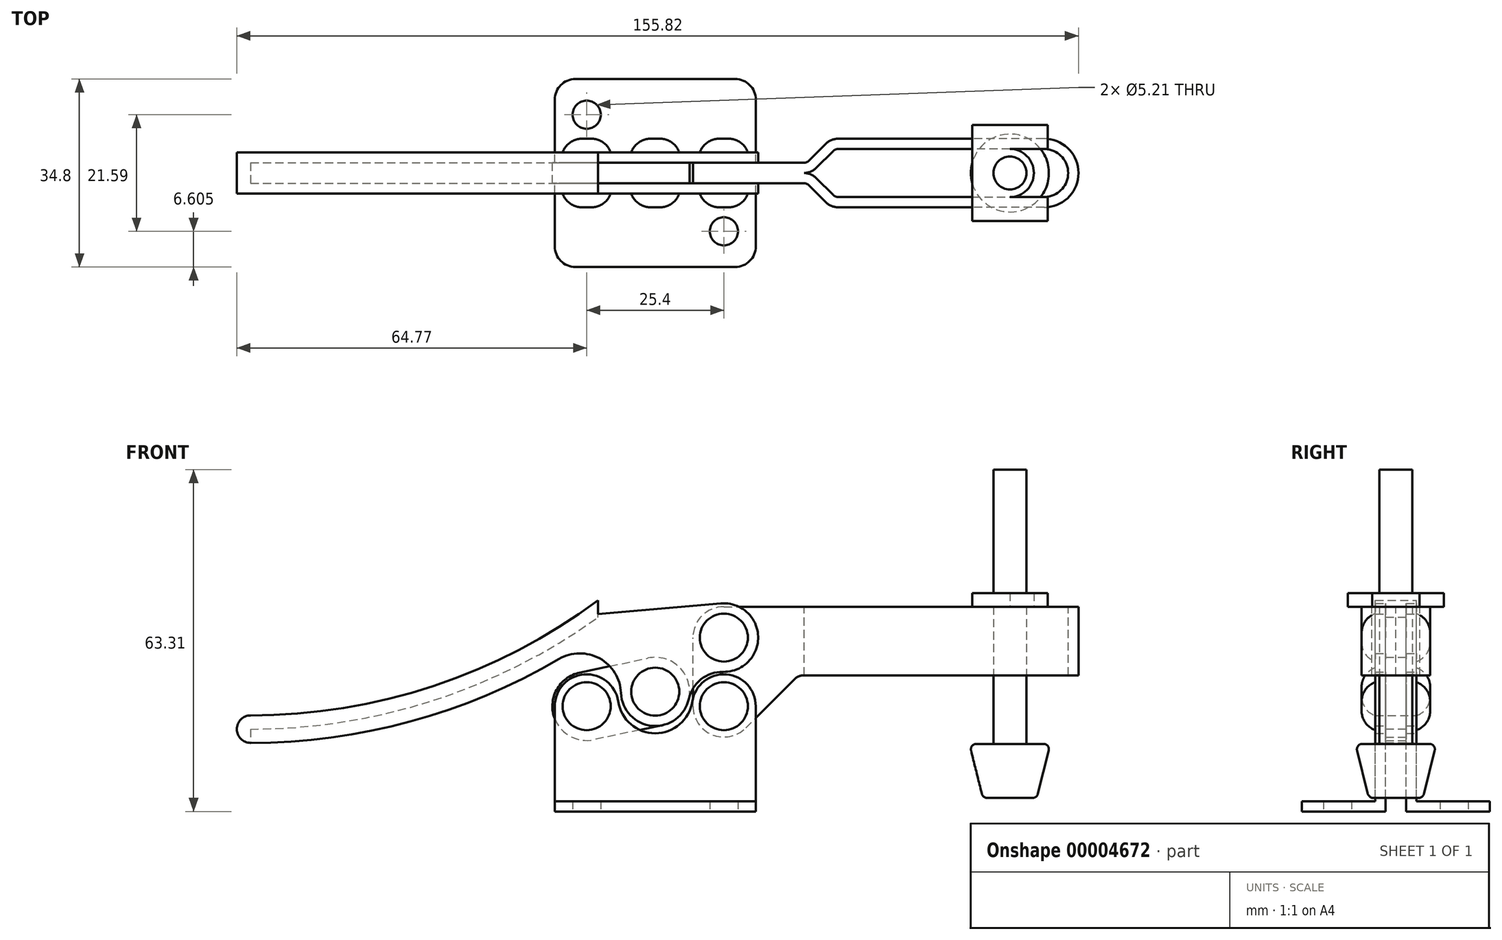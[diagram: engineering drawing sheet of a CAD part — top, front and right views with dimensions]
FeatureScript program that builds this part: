
annotation { "Feature Type Name" : "Feature", "Feature Type Description" : "" }
export const myFeature = defineFeature(function(context is Context, id is Id, definition is map)
    precondition{}
    {
        {
            var Q0;
            Q0=qCreatedBy(makeId("Front.planeOp"),FACE);
            var sketch = newSketch(context, id + "F0", { "sketchPlane" : qUnion([Q0])});
            skLineSegment(sketch, "E0", {"start": v(0, 0) * mm, "end": v(-18.6, 0) * mm});
            skLineSegment(sketch, "E1", {"start": v(-18.6, 0) * mm, "end": v(-18.6, 19.5) * mm});
            skArc(sketch, "E2", {"start": v(-18.6, 19.5) * mm, "mid": v(-13.14, 25.38) * mm, "end": v(-6.86, 20.38) * mm});
            skArc(sketch, "E3", {"start": v(-6.86, 20.38) * mm, "mid": v(-4.52, 16.16) * mm, "end": v(0, 14.48) * mm});
            skArc(sketch, "E4.0.MirrorCS", {"start": v(6.86, 20.38) * mm, "mid": v(4.52, 16.16) * mm, "end": v(0, 14.48) * mm});
            skLineSegment(sketch, "E4.1.MirrorCS", {"start": v(0, 0) * mm, "end": v(18.6, 0) * mm});
            skLineSegment(sketch, "E4.2.MirrorCS", {"start": v(18.6, 0) * mm, "end": v(18.6, 19.5) * mm});
            skArc(sketch, "E4.3.MirrorCS", {"start": v(18.6, 19.5) * mm, "mid": v(13.14, 25.38) * mm, "end": v(6.86, 20.38) * mm});
            skCircle(sketch, "E5", {"center": v(-12.7, 19.5) * mm, "radius": 3.81 * mm});
            skCircle(sketch, "E6.0.MirrorC", {"center": v(12.7, 19.5) * mm, "radius": 3.81 * mm});
            skLineSegment(sketch, "E7", {"start": v(-18.6, 1.9) * mm, "end": v(18.6, 1.9) * mm});
            skSolve(sketch);
        }
        {
            var Q0;
            Q0=qSketchRegion(id+"F0",true);
            extrude(context, id + "F1", {"entities" : qUnion([Q0]), "endBound" : BoundingType.SYMMETRIC, "depth" : 7.62 * mm});
        }
        {
            var Q0;
            {var subQ2=sQuery(id+"F0.wireOp",EDGE,"E0");Q0=makeQuery(id+"F0.imprint","IMPRINT",FACE,{"disambiguationData":[TD([[makeQuery(id+"F0.imprint","IMPRINT",EDGE,{"derivedFrom":subQ2}),-1.0]])]});}
            extrude(context, id + "F2", {"entities" : qUnion([Q0]), "operationType" : NewBodyOperationType.ADD, "endBound" : BoundingType.SYMMETRIC, "depth" : 34.8 * mm});
        }
        {
            var Q0;
            Q0=qSketchRegion(id+"F0",true);
            extrude(context, id + "F3", {"entities" : qUnion([Q0]), "operationType" : NewBodyOperationType.REMOVE, "endBound" : BoundingType.SYMMETRIC, "oppositeDirection" : true, "depth" : 3.8 * mm});
        }
        {
            var Q0;
            Q0=qCreatedBy(makeId("Top.planeOp"),FACE);
            var sketch = newSketch(context, id + "F4", { "sketchPlane" : qUnion([Q0])});
            skCircle(sketch, "E8", {"center": v(-12.7, 10.8) * mm, "radius": 2.6 * mm});
            skArc(sketch, "E9", {"start": v(-14.8, 17.4) * mm, "mid": v(-17.49, 16.28) * mm, "end": v(-18.6, 13.59) * mm});
            skLineSegment(sketch, "E10", {"start": v(-18.6, 13.59) * mm, "end": v(-18.6, 17.4) * mm});
            skLineSegment(sketch, "E11", {"start": v(-18.6, 17.4) * mm, "end": v(-14.8, 17.4) * mm});
            skCircle(sketch, "E12.0.MirrorC", {"center": v(12.7, 10.8) * mm, "radius": 2.6 * mm});
            skLineSegment(sketch, "E12.1.MirrorCS", {"start": v(18.6, 17.4) * mm, "end": v(14.8, 17.4) * mm});
            skLineSegment(sketch, "E12.2.MirrorCS", {"start": v(18.6, 13.59) * mm, "end": v(18.6, 17.4) * mm});
            skArc(sketch, "E12.3.MirrorCS", {"start": v(14.8, 17.4) * mm, "mid": v(17.49, 16.28) * mm, "end": v(18.6, 13.59) * mm});
            skLineSegment(sketch, "E13.0.MirrorCS", {"start": v(-18.6, -13.59) * mm, "end": v(-18.6, -17.4) * mm});
            skArc(sketch, "E13.1.MirrorCS", {"start": v(-14.8, -17.4) * mm, "mid": v(-17.49, -16.28) * mm, "end": v(-18.6, -13.59) * mm});
            skCircle(sketch, "E13.2.MirrorC", {"center": v(12.7, -10.8) * mm, "radius": 2.6 * mm});
            skCircle(sketch, "E13.3.MirrorC", {"center": v(-12.7, -10.8) * mm, "radius": 2.6 * mm});
            skArc(sketch, "E13.4.MirrorCS", {"start": v(14.8, -17.4) * mm, "mid": v(17.49, -16.28) * mm, "end": v(18.6, -13.59) * mm});
            skLineSegment(sketch, "E13.5.MirrorCS", {"start": v(-18.6, -17.4) * mm, "end": v(-14.8, -17.4) * mm});
            skLineSegment(sketch, "E13.6.MirrorCS", {"start": v(18.6, -17.4) * mm, "end": v(14.8, -17.4) * mm});
            skLineSegment(sketch, "E13.7.MirrorCS", {"start": v(18.6, -13.59) * mm, "end": v(18.6, -17.4) * mm});
            skSolve(sketch);
        }
        {
            var Q0;
            Q0=makeQuery(id+"F4.imprint","IMPRINT",FACE,{"disambiguationData":[TD([[makeQuery(id+"F4.imprint","IMPRINT",EDGE,{"derivedFrom":sQuery(id+"F4.wireOp",EDGE,"E8")}),1.0]])]});
            var Q1;
            Q1=makeQuery(id+"F4.imprint","IMPRINT",FACE,{"disambiguationData":[TD([[makeQuery(id+"F4.imprint","IMPRINT",EDGE,{"derivedFrom":sQuery(id+"F4.wireOp",EDGE,"E9")}),-1.0]])]});
            var Q2;
            Q2=makeQuery(id+"F4.imprint","IMPRINT",FACE,{"disambiguationData":[TD([[makeQuery(id+"F4.imprint","IMPRINT",EDGE,{"derivedFrom":sQuery(id+"F4.wireOp",EDGE,"E12.0.MirrorC")}),-1.0]])]});
            var Q3;
            Q3=makeQuery(id+"F4.imprint","IMPRINT",FACE,{"disambiguationData":[TD([[makeQuery(id+"F4.imprint","IMPRINT",EDGE,{"derivedFrom":sQuery(id+"F4.wireOp",EDGE,"E12.1.MirrorCS")}),1.0]])]});
            var Q4;
            Q4=makeQuery(id+"F4.imprint","IMPRINT",FACE,{"disambiguationData":[TD([[makeQuery(id+"F4.imprint","IMPRINT",EDGE,{"derivedFrom":sQuery(id+"F4.wireOp",EDGE,"E13.2.MirrorC")}),1.0]])]});
            var Q5;
            Q5=makeQuery(id+"F4.imprint","IMPRINT",FACE,{"disambiguationData":[TD([[makeQuery(id+"F4.imprint","IMPRINT",EDGE,{"derivedFrom":sQuery(id+"F4.wireOp",EDGE,"E13.4.MirrorCS")}),-1.0]])]});
            var Q6;
            Q6=makeQuery(id+"F4.imprint","IMPRINT",FACE,{"disambiguationData":[TD([[makeQuery(id+"F4.imprint","IMPRINT",EDGE,{"derivedFrom":sQuery(id+"F4.wireOp",EDGE,"E13.0.MirrorCS")}),1.0]])]});
            var Q7;
            Q7=makeQuery(id+"F4.imprint","IMPRINT",FACE,{"disambiguationData":[TD([[makeQuery(id+"F4.imprint","IMPRINT",EDGE,{"derivedFrom":sQuery(id+"F4.wireOp",EDGE,"E13.3.MirrorC")}),-1.0]])]});
            extrude(context, id + "F5", {"entities" : qUnion([Q0, Q1, Q2, Q3, Q4, Q5, Q6, Q7]), "operationType" : NewBodyOperationType.REMOVE, "endBound" : BoundingType.THROUGH_ALL, "depth" : 25.4 * mm});
        }
        {
            var Q0;
            Q0=qCreatedBy(makeId("Front.planeOp"),FACE);
            var sketch = newSketch(context, id + "F6", { "sketchPlane" : qUnion([Q0])});
            skCircle(sketch, "E14", {"center": v(12.7, 19.5) * mm, "radius": 5.72 * mm});
            skLineSegment(sketch, "E15", {"start": v(6.98, 19.5) * mm, "end": v(6.98, 32.2) * mm});
            skCircle(sketch, "E16", {"center": v(12.7, 32.2) * mm, "radius": 5.72 * mm});
            skLineSegment(sketch, "E17", {"start": v(12.7, 37.9) * mm, "end": v(75.8, 37.9) * mm});
            skLineSegment(sketch, "E18", {"start": v(16.74, 15.45) * mm, "end": v(25.75, 24.47) * mm});
            skArc(sketch, "E19", {"start": v(25.75, 24.47) * mm, "mid": v(26.58, 25.02) * mm, "end": v(27.55, 25.2) * mm});
            skLineSegment(sketch, "E20", {"start": v(27.55, 25.2) * mm, "end": v(75.8, 25.2) * mm});
            skLineSegment(sketch, "E21", {"start": v(27.55, 25.2) * mm, "end": v(27.55, 37.9) * mm});
            skArc(sketch, "E22", {"start": v(75.8, 25.2) * mm, "mid": v(77.6, 25.95) * mm, "end": v(78.35, 27.75) * mm});
            skArc(sketch, "E23", {"start": v(75.8, 37.9) * mm, "mid": v(77.6, 37.17) * mm, "end": v(78.35, 35.37) * mm});
            skLineSegment(sketch, "E24", {"start": v(78.35, 35.37) * mm, "end": v(78.35, 27.75) * mm});
            skCircle(sketch, "E25", {"center": v(-12.7, 19.5) * mm, "radius": 3.81 * mm});
            skCircle(sketch, "E26", {"center": v(0, 22.18) * mm, "radius": 3.81 * mm});
            skCircle(sketch, "E27", {"center": v(-12.7, 19.5) * mm, "radius": 6.35 * mm});
            skCircle(sketch, "E28", {"center": v(0, 22.18) * mm, "radius": 6.35 * mm});
            skLineSegment(sketch, "E29", {"start": v(-14.01, 25.7) * mm, "end": v(-1.31, 28.4) * mm});
            skLineSegment(sketch, "E30", {"start": v(1.31, 15.97) * mm, "end": v(-11.39, 13.28) * mm});
            skSolve(sketch);
        }
        {
            var Q0;
            {var subQ0=sQuery(id+"F6.wireOp",EDGE,"E14");var subQ2=makeQuery(id+"F6.imprint","INTERSECT",VERTEX,{"derivedFrom":[subQ0,sQuery(id+"F6.wireOp",EDGE,"E15")]});Q0=makeQuery(id+"F6.imprint","IMPRINT",FACE,{"disambiguationData":[TD([[makeQuery(id+"F6.imprint","IMPRINT",EDGE,{"disambiguationData":[TD([[subQ2,-1.0]])],"derivedFrom":subQ0}),1.0]])]});}
            var Q1;
            {var subQ0=sQuery(id+"F6.wireOp",EDGE,"E16");var subQ2=makeQuery(id+"F6.imprint","INTERSECT",VERTEX,{"derivedFrom":[sQuery(id+"F6.wireOp",EDGE,"E15"),subQ0]});Q1=makeQuery(id+"F6.imprint","IMPRINT",FACE,{"disambiguationData":[TD([[makeQuery(id+"F6.imprint","IMPRINT",EDGE,{"disambiguationData":[TD([[subQ2,1.0]])],"derivedFrom":subQ0}),1.0]])]});}
            var Q2;
            {var subQ5=sQuery(id+"F6.wireOp",EDGE,"E15");Q2=makeQuery(id+"F6.imprint","IMPRINT",FACE,{"disambiguationData":[TD([[makeQuery(id+"F6.imprint","IMPRINT",EDGE,{"derivedFrom":subQ5}),-1.0]])]});}
            var Q3;
            {var subQ1=sQuery(id+"F6.wireOp",EDGE,"E29");Q3=makeQuery(id+"F6.imprint","IMPRINT",FACE,{"disambiguationData":[TD([[makeQuery(id+"F6.imprint","IMPRINT",EDGE,{"derivedFrom":subQ1}),-1.0]])]});}
            var Q4;
            Q4=makeQuery(id+"F6.imprint","IMPRINT",FACE,{"disambiguationData":[TD([[makeQuery(id+"F6.imprint","IMPRINT",EDGE,{"derivedFrom":sQuery(id+"F6.wireOp",EDGE,"E26")}),-1.0]])]});
            var Q5;
            Q5=makeQuery(id+"F6.imprint","IMPRINT",FACE,{"disambiguationData":[TD([[makeQuery(id+"F6.imprint","IMPRINT",EDGE,{"derivedFrom":sQuery(id+"F6.wireOp",EDGE,"E25")}),-1.0]])]});
            extrude(context, id + "F7", {"entities" : qUnion([Q0, Q1, Q2, Q3, Q4, Q5]), "operationType" : NewBodyOperationType.ADD, "endBound" : BoundingType.SYMMETRIC, "depth" : 3.8 * mm});
        }
        {
            var Q0;
            Q0=makeQuery(id+"F7.opExtrude","SWEPT_FACE",FACE,{"disambiguationData":[OSD([sQuery(id+"F6.wireOp",EDGE,"E17")])]});
            var sketch = newSketch(context, id + "F8", { "sketchPlane" : qUnion([Q0])});
            skLineSegment(sketch, "E31", {"start": v(12.7, 1.9) * mm, "end": v(27.55, 1.9) * mm});
            skArc(sketch, "E32", {"start": v(27.55, 1.9) * mm, "mid": v(28.04, 2) * mm, "end": v(28.45, 2.28) * mm});
            skLineSegment(sketch, "E33", {"start": v(27.55, 0) * mm, "end": v(12.7, 0) * mm});
            skArc(sketch, "E34", {"start": v(27.55, 0) * mm, "mid": v(28.76, 0.24) * mm, "end": v(29.8, 0.93) * mm});
            skLineSegment(sketch, "E35", {"start": v(28.45, 2.28) * mm, "end": v(31.6, 5.42) * mm});
            skLineSegment(sketch, "E36", {"start": v(29.8, 0.93) * mm, "end": v(32.94, 4.07) * mm});
            skLineSegment(sketch, "E37", {"start": v(33.84, 4.44) * mm, "end": v(72, 4.44) * mm});
            skLineSegment(sketch, "E38", {"start": v(72, 6.35) * mm, "end": v(33.84, 6.35) * mm});
            skArc(sketch, "E39", {"start": v(32.94, 4.07) * mm, "mid": v(33.35, 4.35) * mm, "end": v(33.84, 4.44) * mm});
            skArc(sketch, "E40", {"start": v(31.6, 5.42) * mm, "mid": v(32.62, 6.1) * mm, "end": v(33.84, 6.35) * mm});
            skArc(sketch, "E41", {"start": v(72, 4.44) * mm, "mid": v(75.14, 3.14) * mm, "end": v(76.44, 0) * mm});
            skArc(sketch, "E42", {"start": v(72, 6.35) * mm, "mid": v(76.49, 4.5) * mm, "end": v(78.35, 0) * mm});
            skLineSegment(sketch, "E43", {"start": v(76.44, 0) * mm, "end": v(78.35, 0) * mm});
            skArc(sketch, "E44.0.MirrorCS", {"start": v(72, -4.45) * mm, "mid": v(75.14, -3.14) * mm, "end": v(76.44, 0) * mm});
            skArc(sketch, "E44.1.MirrorCS", {"start": v(31.6, -5.42) * mm, "mid": v(32.62, -6.1) * mm, "end": v(33.84, -6.35) * mm});
            skLineSegment(sketch, "E44.3.MirrorCS", {"start": v(29.8, -0.93) * mm, "end": v(32.94, -4.07) * mm});
            skArc(sketch, "E44.4.MirrorCS", {"start": v(72, -6.35) * mm, "mid": v(76.49, -4.5) * mm, "end": v(78.35, 0) * mm});
            skArc(sketch, "E44.5.MirrorCS", {"start": v(27.55, -1.9) * mm, "mid": v(28.04, -2) * mm, "end": v(28.45, -2.28) * mm});
            skLineSegment(sketch, "E44.6.MirrorCS", {"start": v(33.84, -4.44) * mm, "end": v(72, -4.44) * mm});
            skLineSegment(sketch, "E44.7.MirrorCS", {"start": v(72, -6.35) * mm, "end": v(33.84, -6.35) * mm});
            skLineSegment(sketch, "E44.8.MirrorCS", {"start": v(28.45, -2.28) * mm, "end": v(31.6, -5.42) * mm});
            skArc(sketch, "E44.9.MirrorCS", {"start": v(32.94, -4.07) * mm, "mid": v(33.35, -4.35) * mm, "end": v(33.84, -4.44) * mm});
            skArc(sketch, "E44.10.MirrorCS", {"start": v(27.55, 0) * mm, "mid": v(28.76, -0.24) * mm, "end": v(29.8, -0.93) * mm});
            skSolve(sketch);
        }
        {
            var Q0;
            Q0=makeQuery(id+"F8.imprint","IMPRINT",FACE,{"disambiguationData":[TD([[makeQuery(id+"F8.imprint","IMPRINT",EDGE,{"derivedFrom":sQuery(id+"F8.wireOp",EDGE,"E44.0.MirrorCS")}),-1.0]])]});
            var Q1;
            {var subQ2=sQuery(id+"F8.wireOp",EDGE,"E32");Q1=makeQuery(id+"F8.imprint","IMPRINT",FACE,{"disambiguationData":[TD([[makeQuery(id+"F8.imprint","IMPRINT",EDGE,{"derivedFrom":subQ2}),-1.0]])]});}
            var Q2;
            Q2=makeQuery(id+"F8.imprint","IMPRINT",FACE,{"disambiguationData":[TD([[makeQuery(id+"F8.imprint","IMPRINT",EDGE,{"derivedFrom":sQuery(id+"F8.wireOp",EDGE,"E34")}),-1.0]])]});
            extrude(context, id + "F9", {"entities" : qUnion([Q0, Q1, Q2]), "operationType" : NewBodyOperationType.ADD, "oppositeDirection" : true, "depth" : 12.7 * mm});
        }
        {
            var Q0;
            Q0=makeQuery(id+"F8.imprint","IMPRINT",FACE,{"disambiguationData":[TD([[makeQuery(id+"F8.imprint","IMPRINT",EDGE,{"derivedFrom":sQuery(id+"F8.wireOp",EDGE,"E34")}),-1.0]])]});
            extrude(context, id + "F10", {"entities" : qUnion([Q0]), "operationType" : NewBodyOperationType.REMOVE, "endBound" : BoundingType.THROUGH_ALL, "oppositeDirection" : true, "depth" : 25.4 * mm});
        }
        {
            var Q0;
            Q0=qCreatedBy(makeId("Front.planeOp"),FACE);
            var sketch = newSketch(context, id + "F11", { "sketchPlane" : qUnion([Q0])});
            skCircle(sketch, "E45", {"center": v(12.7, 32.2) * mm, "radius": 6.35 * mm});
            skCircle(sketch, "E46", {"center": v(0, 22.18) * mm, "radius": 6.35 * mm});
            skArc(sketch, "E47", {"start": v(12.56, 25.85) * mm, "mid": v(8.48, 24.48) * mm, "end": v(6.2, 20.84) * mm});
            skArc(sketch, "E48", {"start": v(-6.35, 21.94) * mm, "mid": v(-10.3, 28.33) * mm, "end": v(-17.82, 28.22) * mm});
            skArc(sketch, "E49", {"start": v(-17.82, 28.22) * mm, "mid": v(-45.34, 16.65) * mm, "end": v(-74.93, 12.7) * mm});
            skArc(sketch, "E50", {"start": v(-74.93, 12.7) * mm, "mid": v(-77.47, 15.24) * mm, "end": v(-74.93, 17.78) * mm});
            skArc(sketch, "E51", {"start": v(-74.93, 17.78) * mm, "mid": v(-41.06, 23.24) * mm, "end": v(-10.63, 39.07) * mm});
            skLineSegment(sketch, "E52", {"start": v(12.15, 38.52) * mm, "end": v(-10.63, 36.53) * mm});
            skLineSegment(sketch, "E53", {"start": v(-10.63, 36.53) * mm, "end": v(-10.63, 39.07) * mm});
            skArc(sketch, "E54", {"start": v(-74.93, 15.24) * mm, "mid": v(-41.16, 20.54) * mm, "end": v(-10.63, 35.92) * mm});
            skLineSegment(sketch, "E55", {"start": v(-10.63, 36.53) * mm, "end": v(-10.63, 35.92) * mm});
            skLineSegment(sketch, "E56", {"start": v(-74.93, 15.24) * mm, "end": v(-74.93, 17.78) * mm});
            skLineSegment(sketch, "E57", {"start": v(6.33, 22.73) * mm, "end": v(5, 37.9) * mm});
            skLineSegment(sketch, "E58", {"start": v(15.47, 37.9) * mm, "end": v(12.7, 37.9) * mm});
            skLineSegment(sketch, "E59", {"start": v(6.98, 29.43) * mm, "end": v(6.98, 32.2) * mm});
            skArc(sketch, "E60", {"start": v(12.7, 37.9) * mm, "mid": v(8.66, 36.24) * mm, "end": v(6.99, 32.2) * mm});
            skLineSegment(sketch, "E61", {"start": v(6.98, 29.43) * mm, "end": v(6.98, 22.8) * mm});
            skSolve(sketch);
        }
        {
            var Q0;
            {var subQ0=sQuery(id+"F11.wireOp",EDGE,"E46");var subQ3=makeQuery(id+"F11.imprint","INTERSECT",VERTEX,{"derivedFrom":[subQ0,sQuery(id+"F11.wireOp",EDGE,"E48")]});Q0=makeQuery(id+"F11.imprint","IMPRINT",FACE,{"disambiguationData":[TD([[makeQuery(id+"F11.imprint","IMPRINT",EDGE,{"disambiguationData":[TD([[subQ3,1.0]])],"derivedFrom":subQ0}),1.0]])]});}
            var Q1;
            Q1=makeQuery(id+"F11.imprint","IMPRINT",FACE,{"disambiguationData":[TD([[makeQuery(id+"F11.imprint","IMPRINT",EDGE,{"derivedFrom":sQuery(id+"F11.wireOp",EDGE,"E51")}),-1.0]])]});
            var Q2;
            {var subQ3=sQuery(id+"F11.wireOp",EDGE,"E48");Q2=makeQuery(id+"F11.imprint","IMPRINT",FACE,{"disambiguationData":[TD([[makeQuery(id+"F11.imprint","IMPRINT",EDGE,{"derivedFrom":subQ3}),-1.0]])]});}
            var Q3;
            {var subQ0=sQuery(id+"F11.wireOp",EDGE,"E61");Q3=makeQuery(id+"F11.imprint","IMPRINT",FACE,{"disambiguationData":[TD([[makeQuery(id+"F11.imprint","IMPRINT",EDGE,{"derivedFrom":subQ0}),1.0]])]});}
            var Q4;
            {var subQ1=sQuery(id+"F11.wireOp",EDGE,"E58");Q4=makeQuery(id+"F11.imprint","IMPRINT",FACE,{"disambiguationData":[TD([[makeQuery(id+"F11.imprint","IMPRINT",EDGE,{"derivedFrom":subQ1}),1.0]])]});}
            var Q5;
            {var subQ1=sQuery(id+"F11.wireOp",EDGE,"E58");Q5=makeQuery(id+"F11.imprint","IMPRINT",FACE,{"disambiguationData":[TD([[makeQuery(id+"F11.imprint","IMPRINT",EDGE,{"derivedFrom":subQ1}),-1.0]])]});}
            var Q6;
            {var subQ1=sQuery(id+"F11.wireOp",EDGE,"E57");Q6=makeQuery(id+"F11.imprint","IMPRINT",FACE,{"disambiguationData":[TD([[makeQuery(id+"F11.imprint","IMPRINT",EDGE,{"derivedFrom":subQ1}),-1.0]])]});}
            extrude(context, id + "F12", {"entities" : qUnion([Q0, Q1, Q2, Q3, Q4, Q5, Q6]), "operationType" : NewBodyOperationType.ADD, "endBound" : BoundingType.SYMMETRIC, "depth" : 7.62 * mm});
        }
        {
            var Q0;
            Q0=qCreatedBy(makeId("Front.planeOp"),FACE);
            var sketch = newSketch(context, id + "F13", { "sketchPlane" : qUnion([Q0])});
            skCircle(sketch, "E62", {"center": v(12.7, 32.2) * mm, "radius": 4.45 * mm});
            skCircle(sketch, "E63", {"center": v(12.7, 19.5) * mm, "radius": 4.45 * mm});
            skCircle(sketch, "E64", {"center": v(0, 22.18) * mm, "radius": 4.45 * mm});
            skCircle(sketch, "E65", {"center": v(-12.7, 19.5) * mm, "radius": 4.45 * mm});
            skSolve(sketch);
        }
        {
            var Q0;
            {Q0=qUnion([makeQuery(id+"F13.imprint","IMPRINT",FACE,{"disambiguationData":[TD([[makeQuery(id+"F13.imprint","IMPRINT",EDGE,{"derivedFrom":sQuery(id+"F13.wireOp",EDGE,"E62")}),1.0]])]}),makeQuery(id+"F13.imprint","IMPRINT",FACE,{"disambiguationData":[TD([[makeQuery(id+"F13.imprint","IMPRINT",EDGE,{"derivedFrom":sQuery(id+"F13.wireOp",EDGE,"E63")}),1.0]])]}),makeQuery(id+"F13.imprint","IMPRINT",FACE,{"disambiguationData":[TD([[makeQuery(id+"F13.imprint","IMPRINT",EDGE,{"derivedFrom":sQuery(id+"F13.wireOp",EDGE,"E64")}),1.0]])]}),makeQuery(id+"F13.imprint","IMPRINT",FACE,{"disambiguationData":[TD([[makeQuery(id+"F13.imprint","IMPRINT",EDGE,{"derivedFrom":sQuery(id+"F13.wireOp",EDGE,"E65")}),1.0]])]})]);}
            extrude(context, id + "F14", {"entities" : qUnion([Q0]), "operationType" : NewBodyOperationType.ADD, "endBound" : BoundingType.SYMMETRIC, "depth" : 12.7 * mm});
        }
        {
            var Q0;
            Q0=qCreatedBy(makeId("Front.planeOp"),FACE);
            var sketch = newSketch(context, id + "F15", { "sketchPlane" : qUnion([Q0])});
            skLineSegment(sketch, "E66", {"start": v(-8.43, 26.89) * mm, "end": v(-1.31, 28.4) * mm});
            skArc(sketch, "E67", {"start": v(6.2, 20.84) * mm, "mid": v(4.5, 26.66) * mm, "end": v(-1.31, 28.4) * mm});
            skArc(sketch, "E68", {"start": v(6.98, 22.8) * mm, "mid": v(6.51, 21.85) * mm, "end": v(6.2, 20.84) * mm});
            skLineSegment(sketch, "E69", {"start": v(6.98, 22.8) * mm, "end": v(6.98, 32.2) * mm});
            skArc(sketch, "E70", {"start": v(12.7, 37.9) * mm, "mid": v(8.66, 36.24) * mm, "end": v(6.99, 32.2) * mm});
            skLineSegment(sketch, "E71", {"start": v(12.7, 37.9) * mm, "end": v(15.47, 37.9) * mm});
            skArc(sketch, "E72", {"start": v(15.47, 37.9) * mm, "mid": v(13.85, 38.44) * mm, "end": v(12.15, 38.52) * mm});
            skLineSegment(sketch, "E73", {"start": v(12.15, 38.52) * mm, "end": v(-10.63, 36.53) * mm});
            skLineSegment(sketch, "E74", {"start": v(-10.63, 35.92) * mm, "end": v(-10.63, 36.53) * mm});
            skArc(sketch, "E75", {"start": v(-8.43, 26.89) * mm, "mid": v(-12.89, 29.2) * mm, "end": v(-17.82, 28.22) * mm});
            skArc(sketch, "E76", {"start": v(-74.93, 15.24) * mm, "mid": v(-41.16, 20.54) * mm, "end": v(-10.63, 35.92) * mm});
            skArc(sketch, "E77", {"start": v(-74.93, 12.7) * mm, "mid": v(-45.34, 16.65) * mm, "end": v(-17.82, 28.22) * mm});
            skLineSegment(sketch, "E78", {"start": v(-74.93, 15.24) * mm, "end": v(-74.93, 12.7) * mm});
            skSolve(sketch);
        }
        {
            var Q0;
            Q0=makeQuery(id+"F15.imprint","IMPRINT",FACE,{"disambiguationData":[TD([[makeQuery(id+"F15.imprint","IMPRINT",EDGE,{"derivedFrom":sQuery(id+"F15.wireOp",EDGE,"E66")}),1.0]])]});
            extrude(context, id + "F16", {"entities" : qUnion([Q0]), "operationType" : NewBodyOperationType.REMOVE, "endBound" : BoundingType.SYMMETRIC, "oppositeDirection" : true, "depth" : 3.8 * mm});
        }
        {
            var Q0;
            Q0=makeQuery(id+"F14.opExtrude","CAP_FACE",FACE,{"disambiguationData":[OSD([sQuery(id+"F13.wireOp",EDGE,"E65")])],"isStart":false});
            var Q1;
            Q1=makeQuery(id+"F14.opExtrude","CAP_FACE",FACE,{"disambiguationData":[OSD([sQuery(id+"F13.wireOp",EDGE,"E64")])],"isStart":false});
            var Q2;
            Q2=makeQuery(id+"F14.opExtrude","CAP_FACE",FACE,{"disambiguationData":[OSD([sQuery(id+"F13.wireOp",EDGE,"E63")])],"isStart":false});
            var Q3;
            Q3=makeQuery(id+"F14.opExtrude","CAP_FACE",FACE,{"disambiguationData":[OSD([sQuery(id+"F13.wireOp",EDGE,"E62")])],"isStart":false});
            var Q4;
            Q4=makeQuery(id+"F14.opExtrude","CAP_FACE",FACE,{"disambiguationData":[OSD([sQuery(id+"F13.wireOp",EDGE,"E62")])],"isStart":true});
            var Q5;
            Q5=makeQuery(id+"F14.opExtrude","CAP_FACE",FACE,{"disambiguationData":[OSD([sQuery(id+"F13.wireOp",EDGE,"E63")])],"isStart":true});
            var Q6;
            Q6=makeQuery(id+"F14.opExtrude","CAP_FACE",FACE,{"disambiguationData":[OSD([sQuery(id+"F13.wireOp",EDGE,"E64")])],"isStart":true});
            var Q7;
            Q7=makeQuery(id+"F14.opExtrude","CAP_FACE",FACE,{"disambiguationData":[OSD([sQuery(id+"F13.wireOp",EDGE,"E65")])],"isStart":true});
            fillet(context, id + "F17", {"entities" : qUnion([Q0, Q1, Q2, Q3, Q4, Q5, Q6, Q7]), "radius" : 3.8 * mm, "tangentPropagation" : true, "allowEdgeOverflow" : false});
        }
        {
            var Q0;
            {var subQ0=sQuery(id+"F6.wireOp",EDGE,"E17");Q0=makeQuery(id+"F16.boolean.opBoolean","MERGE",FACE,{"derivedFrom":[makeQuery(id+"F9.boolean.opBoolean","MERGE",FACE,{"derivedFrom":[makeQuery(id+"F7.opExtrude","SWEPT_FACE",FACE,{"disambiguationData":[OSD([subQ0])]}),makeQuery(id+"F9.opExtrude","CAP_FACE",FACE,{"disambiguationData":[OSD([subQ0,sQuery(id+"F6.wireOp",EDGE,"E21"),sQuery(id+"F8.wireOp",EDGE,"E32"),sQuery(id+"F8.wireOp",EDGE,"E35"),sQuery(id+"F8.wireOp",EDGE,"E38"),sQuery(id+"F8.wireOp",EDGE,"E40"),sQuery(id+"F8.wireOp",EDGE,"E42"),sQuery(id+"F8.wireOp",EDGE,"E44.1.MirrorCS"),sQuery(id+"F8.wireOp",EDGE,"E44.4.MirrorCS"),sQuery(id+"F8.wireOp",EDGE,"E44.5.MirrorCS"),sQuery(id+"F8.wireOp",EDGE,"E44.7.MirrorCS"),sQuery(id+"F8.wireOp",EDGE,"E44.8.MirrorCS")])],"isStart":true})]}),makeQuery(id+"F16.opExtrude","SWEPT_FACE",FACE,{"disambiguationData":[OSD([sQuery(id+"F15.wireOp",EDGE,"E71")])]})]});}
            var sketch = newSketch(context, id + "F18", { "sketchPlane" : qUnion([Q0])});
            skCircle(sketch, "E79", {"center": v(65.65, 0) * mm, "radius": 4.44 * mm});
            skCircle(sketch, "E80", {"center": v(65.65, 0) * mm, "radius": 3.05 * mm});
            skLineSegment(sketch, "E81", {"start": v(65.65, -4.44) * mm, "end": v(65.65, 4.44) * mm});
            skLineSegment(sketch, "E82.rect.bottom", {"start": v(58.66, -8.89) * mm, "end": v(72.63, -8.89) * mm});
            skLineSegment(sketch, "E82.rect.top", {"start": v(58.66, 8.89) * mm, "end": v(72.63, 8.89) * mm});
            skLineSegment(sketch, "E82.rect.left", {"start": v(58.66, -8.89) * mm, "end": v(58.66, 8.89) * mm});
            skLineSegment(sketch, "E82.rect.right", {"start": v(72.63, -8.89) * mm, "end": v(72.63, 8.89) * mm});
            skSolve(sketch);
        }
        {
            var Q0;
            {var subQ0=sQuery(id+"F18.wireOp",EDGE,"E81");var subQ1=sQuery(id+"F18.wireOp",EDGE,"E80");var subQ3=makeQuery(id+"F18.imprint","INTERSECT",VERTEX,{"disambiguationData":[OD(0.0)],"derivedFrom":[subQ1,subQ0]});Q0=makeQuery(id+"F18.imprint","IMPRINT",FACE,{"disambiguationData":[TD([[makeQuery(id+"F18.imprint","IMPRINT",EDGE,{"disambiguationData":[TD([[subQ3,1.0]])],"derivedFrom":subQ1}),1.0]])]});}
            var Q1;
            {var subQ0=sQuery(id+"F18.wireOp",EDGE,"E81");var subQ1=sQuery(id+"F18.wireOp",EDGE,"E80");var subQ3=makeQuery(id+"F18.imprint","INTERSECT",VERTEX,{"disambiguationData":[OD(0.0)],"derivedFrom":[subQ1,subQ0]});Q1=makeQuery(id+"F18.imprint","IMPRINT",FACE,{"disambiguationData":[TD([[makeQuery(id+"F18.imprint","IMPRINT",EDGE,{"disambiguationData":[TD([[subQ3,-1.0]])],"derivedFrom":subQ1}),1.0]])]});}
            extrude(context, id + "F19", {"entities" : qUnion([Q0, Q1]), "operationType" : NewBodyOperationType.ADD, "endBound" : BoundingType.SYMMETRIC, "depth" : 50.8 * mm});
        }
        {
            var Q0;
            Q0=makeQuery(id+"F19.opExtrude","CAP_FACE",FACE,{"disambiguationData":[OSD([sQuery(id+"F18.wireOp",EDGE,"E80")])],"isStart":true});
            var sketch = newSketch(context, id + "F20", { "sketchPlane" : qUnion([Q0])});
            skLineSegment(sketch, "E83", {"start": v(65.65, 0) * mm, "end": v(62.6, 0) * mm});
            skSolve(sketch);
        }
        {
            var Q0;
            Q0=qCreatedBy(makeId("Front.planeOp"),FACE);
            var sketch = newSketch(context, id + "F21", { "sketchPlane" : qUnion([Q0])});
            skLineSegment(sketch, "E84", {"start": v(65.65, 12.5) * mm, "end": v(58.15, 12.5) * mm});
            skLineSegment(sketch, "E85", {"start": v(58.15, 12.5) * mm, "end": v(60.65, 2.5) * mm});
            skLineSegment(sketch, "E86", {"start": v(60.65, 2.5) * mm, "end": v(65.65, 2.5) * mm});
            skLineSegment(sketch, "E87", {"start": v(65.65, 2.5) * mm, "end": v(65.65, 12.5) * mm});
            skSolve(sketch);
        }
        {
            var Q0;
            Q0=makeQuery(id+"F21.imprint","IMPRINT",FACE,{"disambiguationData":[TD([[makeQuery(id+"F21.imprint","IMPRINT",EDGE,{"derivedFrom":sQuery(id+"F21.wireOp",EDGE,"E84")}),1.0]])]});
            var Q1;
            Q1=sQuery(id+"F21.wireOp",EDGE,"E87");
            revolve(context, id + "F22", {"operationType" : NewBodyOperationType.ADD, "entities" : qUnion([Q0]), "axis" : qUnion([Q1]), "revolveType" : RevolveType.FULL});
        }
        {
            var Q0;
            Q0=makeQuery(id+"F22.opRevolve","SWEPT_EDGE",EDGE,{"disambiguationData":[OSD([sQuery(id+"F21.wireOp",EDGE,"E84"),sQuery(id+"F21.wireOp",EDGE,"E85")])]});
            var Q1;
            Q1=makeQuery(id+"F22.opRevolve","SWEPT_EDGE",EDGE,{"disambiguationData":[OSD([sQuery(id+"F21.wireOp",EDGE,"E85"),sQuery(id+"F21.wireOp",EDGE,"E86")])]});
            fillet(context, id + "F23", {"entities" : qUnion([Q0, Q1]), "radius" : 1 * mm, "tangentPropagation" : true, "allowEdgeOverflow" : false});
        }
        {
            var Q0;
            {var subQ7=sQuery(id+"F18.wireOp",EDGE,"E82.rect.bottom");Q0=makeQuery(id+"F18.imprint","IMPRINT",FACE,{"disambiguationData":[TD([[makeQuery(id+"F18.imprint","IMPRINT",EDGE,{"derivedFrom":subQ7}),1.0]])]});}
            var Q1;
            {var subQ0=makeQuery(id+"F10.boolean.opBoolean","COPY",EDGE,{"derivedFrom":makeQuery(id+"F10.opExtrude","CAP_EDGE",EDGE,{"disambiguationData":[OSD([sQuery(id+"F8.wireOp",EDGE,"E44.6.MirrorCS")])],"isStart":true})});var subQ1=sQuery(id+"F18.wireOp",EDGE,"E82.rect.left");var subQ2=makeQuery(id+"F18.imprint","INTERSECT",VERTEX,{"derivedFrom":[subQ0,subQ1]});Q1=makeQuery(id+"F18.imprint","IMPRINT",FACE,{"disambiguationData":[TD([[makeQuery(id+"F18.imprint","IMPRINT",EDGE,{"disambiguationData":[TD([[subQ2,-1.0]])],"derivedFrom":subQ1}),-1.0]])]});}
            var Q2;
            {var subQ1=sQuery(id+"F18.wireOp",EDGE,"E82.rect.left");var subQ8=makeQuery(id+"F9.opExtrude","CAP_EDGE",EDGE,{"disambiguationData":[OSD([sQuery(id+"F8.wireOp",EDGE,"E44.7.MirrorCS")])],"isStart":true});var subQ9=makeQuery(id+"F18.imprint","INTERSECT",VERTEX,{"derivedFrom":[subQ8,subQ1]});Q2=makeQuery(id+"F18.imprint","IMPRINT",FACE,{"disambiguationData":[TD([[makeQuery(id+"F18.imprint","IMPRINT",EDGE,{"disambiguationData":[TD([[subQ9,-1.0]])],"derivedFrom":subQ1}),-1.0]])]});}
            var Q3;
            {var subQ0=makeQuery(id+"F10.boolean.opBoolean","COPY",EDGE,{"derivedFrom":makeQuery(id+"F10.opExtrude","CAP_EDGE",EDGE,{"disambiguationData":[OSD([sQuery(id+"F8.wireOp",EDGE,"E44.6.MirrorCS")])],"isStart":true})});var subQ1=sQuery(id+"F18.wireOp",EDGE,"E79");var subQ2=sQuery(id+"F18.wireOp",EDGE,"E81");var subQ3=makeQuery(id+"F18.imprint","INTERSECT",VERTEX,{"derivedFrom":[subQ0,subQ1,subQ2]});Q3=makeQuery(id+"F18.imprint","IMPRINT",FACE,{"disambiguationData":[TD([[makeQuery(id+"F18.imprint","IMPRINT",EDGE,{"disambiguationData":[TD([[subQ3,-1.0]])],"derivedFrom":subQ1}),-1.0]])]});}
            var Q4;
            {var subQ0=sQuery(id+"F18.wireOp",EDGE,"E81");var subQ1=sQuery(id+"F18.wireOp",EDGE,"E80");var subQ5=makeQuery(id+"F18.imprint","INTERSECT",VERTEX,{"disambiguationData":[OD(0.0)],"derivedFrom":[subQ1,subQ0]});Q4=makeQuery(id+"F18.imprint","IMPRINT",FACE,{"disambiguationData":[TD([[makeQuery(id+"F18.imprint","IMPRINT",EDGE,{"disambiguationData":[TD([[subQ5,-1.0]])],"derivedFrom":subQ1}),-1.0]])]});}
            var Q5;
            {var subQ0=sQuery(id+"F18.wireOp",EDGE,"E81");var subQ1=sQuery(id+"F18.wireOp",EDGE,"E80");var subQ5=makeQuery(id+"F18.imprint","INTERSECT",VERTEX,{"disambiguationData":[OD(0.0)],"derivedFrom":[subQ1,subQ0]});Q5=makeQuery(id+"F18.imprint","IMPRINT",FACE,{"disambiguationData":[TD([[makeQuery(id+"F18.imprint","IMPRINT",EDGE,{"disambiguationData":[TD([[subQ5,1.0]])],"derivedFrom":subQ1}),-1.0]])]});}
            var Q6;
            {var subQ5=sQuery(id+"F18.wireOp",EDGE,"E82.rect.left");var subQ10=makeQuery(id+"F9.opExtrude","CAP_EDGE",EDGE,{"disambiguationData":[OSD([sQuery(id+"F8.wireOp",EDGE,"E38")])],"isStart":true});var subQ12=makeQuery(id+"F18.imprint","INTERSECT",VERTEX,{"derivedFrom":[subQ10,subQ5]});Q6=makeQuery(id+"F18.imprint","IMPRINT",FACE,{"disambiguationData":[TD([[makeQuery(id+"F18.imprint","IMPRINT",EDGE,{"disambiguationData":[TD([[subQ12,1.0]])],"derivedFrom":subQ5}),-1.0]])]});}
            var Q7;
            {var subQ7=sQuery(id+"F18.wireOp",EDGE,"E82.rect.top");Q7=makeQuery(id+"F18.imprint","IMPRINT",FACE,{"disambiguationData":[TD([[makeQuery(id+"F18.imprint","IMPRINT",EDGE,{"derivedFrom":subQ7}),-1.0]])]});}
            extrude(context, id + "F24", {"entities" : qUnion([Q0, Q1, Q2, Q3, Q4, Q5, Q6, Q7]), "operationType" : NewBodyOperationType.ADD, "depth" : 2.54 * mm});
        }
    });
